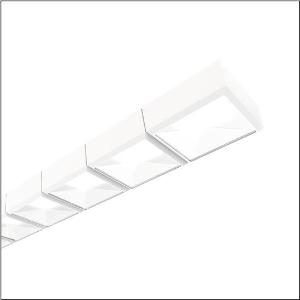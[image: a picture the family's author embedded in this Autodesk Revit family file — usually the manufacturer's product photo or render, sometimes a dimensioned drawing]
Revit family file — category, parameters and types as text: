
# Revit family: scriptus_r__11_5mz214d0twa_b782
name_source: partatom
category: Lighting Fixtures
units: mm (PartAtom-declared; Revit-internal decimal feet)

## family parameters
Cut with Voids When Loaded = No
Host = Face
Light Source = No
Part Type = Normal
Room Calculation Point = No
Round Connector Dimension = Use Diameter
Shared = No

## types (1)
- --- (1 x LED 3000K+6500K / CRI = 80 (unbekannt), 3600 lm, 3000K)
    Apparent Load = 53 VA
    CIE Flux Codes = 82 95 99 100 100
    Color Rendering = 80
    Color Temperature = 3000K
    Default Elevation = 1800 mm
    Description = Scriptus® 11, office luminaire, primary optical cover: lenses, CAT 2 (L<= 3000cd/m²), light emission: direct distribution, primary light characteristic: symmetric, installation type: surface-mounted, LED, rated luminous flux: 7.190lm, luminous efficacy: 137lm/W, light colour: 8tw, colour temperature: 3000..6500K, control gear: ECG DALI, with terminal, 5-pole, mains connection: 230V, AC, 50Hz, rated input power: 53W, housing, luminaire housing, of aluminium, traffic white (RAL 9016), length: 3.088mm, width: 114mm, height: 57mm, protection rating (complete): IP20, insulation class (complete): insulation class I (protective earthing), certification: CE, protection symbol: F, permissible operating ambient temperature: 0..+35°C, standard: EN 50419, packaging unit: 1 piece
    Height = 57 mm
    Lamp = 1 x LED 3000K+6500K / CRI >= 80 (unbekannt)
    Lamp Light Flux = 3600 lm
    Lamp count = 1
    Length = 3088 mm
    Luminous efficacy = 137 lm/W
    Manufacturer = Siteco
    ModVariant = No
    Model = 5MZ214D0TWA
    Mounting Place = Ceiling
    Mounting Type = Surface mounted
    Number of Poles = 1
    OnlyDefault = Yes
    Power Factor = 1
    Product Name = Scriptus® 11
    Product group = office luminaire | ceiling mounted
    ProductGroupID = 300
    Protection Class = Protection class I
    Protection Degree = IP 20
    RLX_Detail_Level = 1
    RLX_Emergency_Light_Flux = 0 lm
    RLX_Emergency_Type = 0
    RLX_Emergency_Type_DB = No
    RlxData = <blob elided: 30429 chars, md5=67d5c58a>
    Socket = socket
    Standby Power = 0 W
    System Light Flux = 7200 lm
    System Power = 53 W
    Type Comments = individual setting: colour temperature 6500K
    Type Image = l_1004833.jpg
    URL = http://relux.com
    VarID = @adj_164761
    Voltage = 0 V
    Weight = 0.00 kg
    Width = 114 mm

## geometry (parser evidence)
native form markers: Blend x4, Sweep x14
no freeform markers — native parametric forms only
